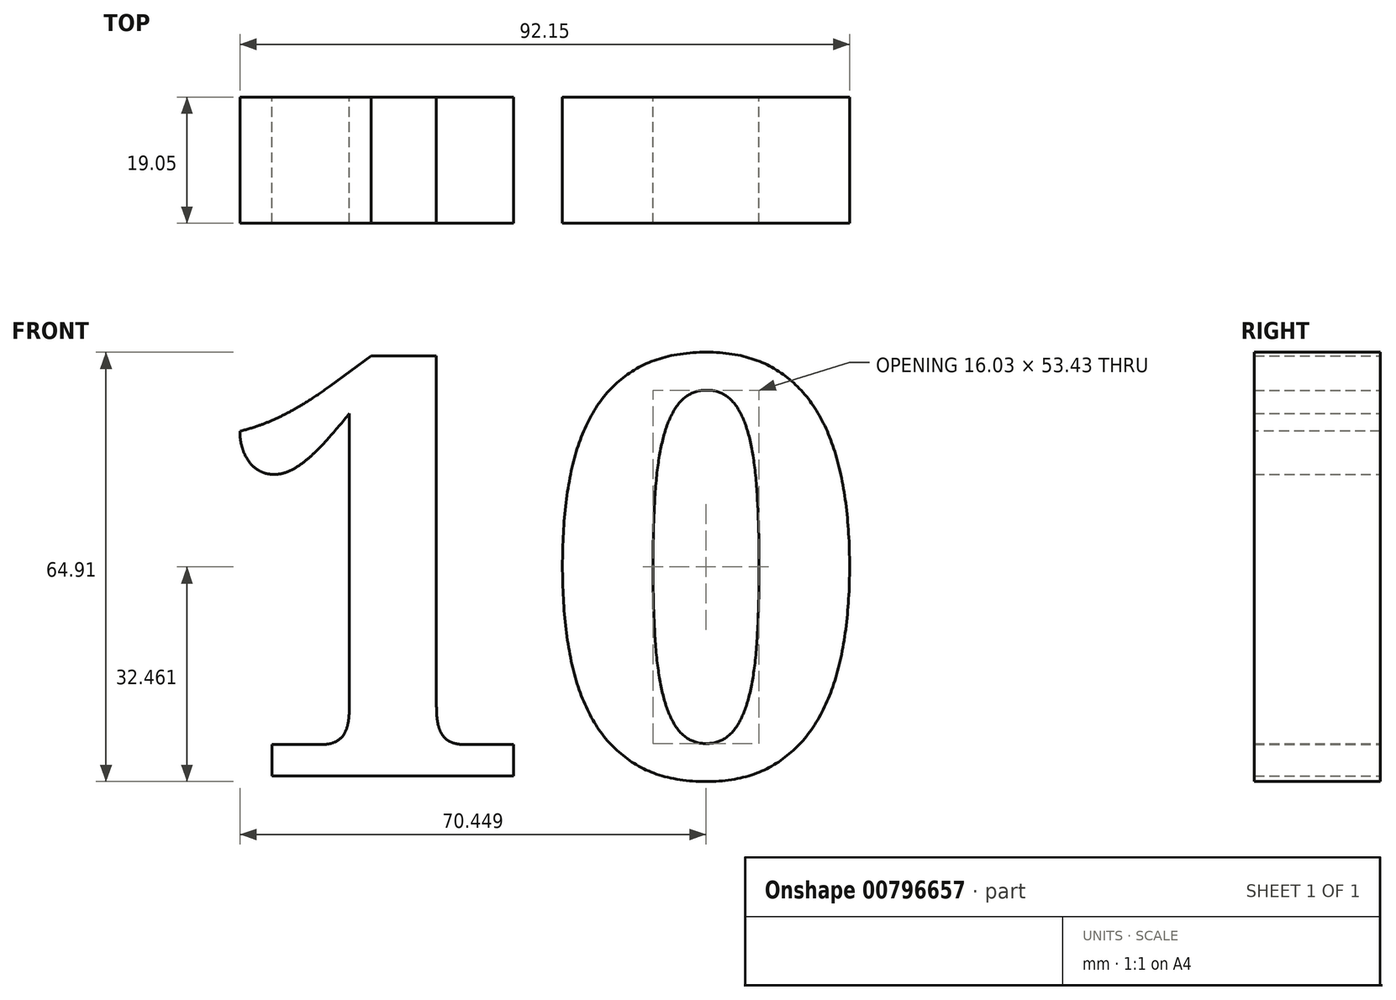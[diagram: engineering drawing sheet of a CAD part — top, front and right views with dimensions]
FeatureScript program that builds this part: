
annotation { "Feature Type Name" : "Feature", "Feature Type Description" : "" }
export const myFeature = defineFeature(function(context is Context, id is Id, definition is map)
    precondition{}
    {
        {
            var Q0;
            Q0=qCreatedBy(makeId("Front.planeOp"),FACE);
            var sketch = newSketch(context, id + "F0", { "sketchPlane" : qUnion([Q0])});
            skText(sketch, "E0", { "text": "10", "fontName": "NotoSerif-Bold.ttf"});
            const initialGuessF0  = {"E0": [0, 0, 1, 0, 0.06368]};
            skSetInitialGuess(sketch, initialGuessF0);
            skSolve(sketch);
        }
        {
            var Q0;
            Q0=makeQuery(id+"F0.imprint","IMPRINT",FACE,{"disambiguationData":[TD([[makeQuery(id+"F0.imprint","IMPRINT",EDGE,{"derivedFrom":sQuery(id+"F0.wireOp",EDGE,"E0.sketch_text.stroke-0")}),-1.0]])]});
            var Q1;
            Q1=makeQuery(id+"F0.imprint","IMPRINT",FACE,{"disambiguationData":[TD([[makeQuery(id+"F0.imprint","IMPRINT",EDGE,{"derivedFrom":sQuery(id+"F0.wireOp",EDGE,"E0.sketch_text.stroke-29")}),-1.0]])]});
            extrude(context, id + "F1", {"entities" : qUnion([Q0, Q1]), "depth" : 19.05 * mm, "offsetDistance" : 25.4 * mm});
        }
    });
